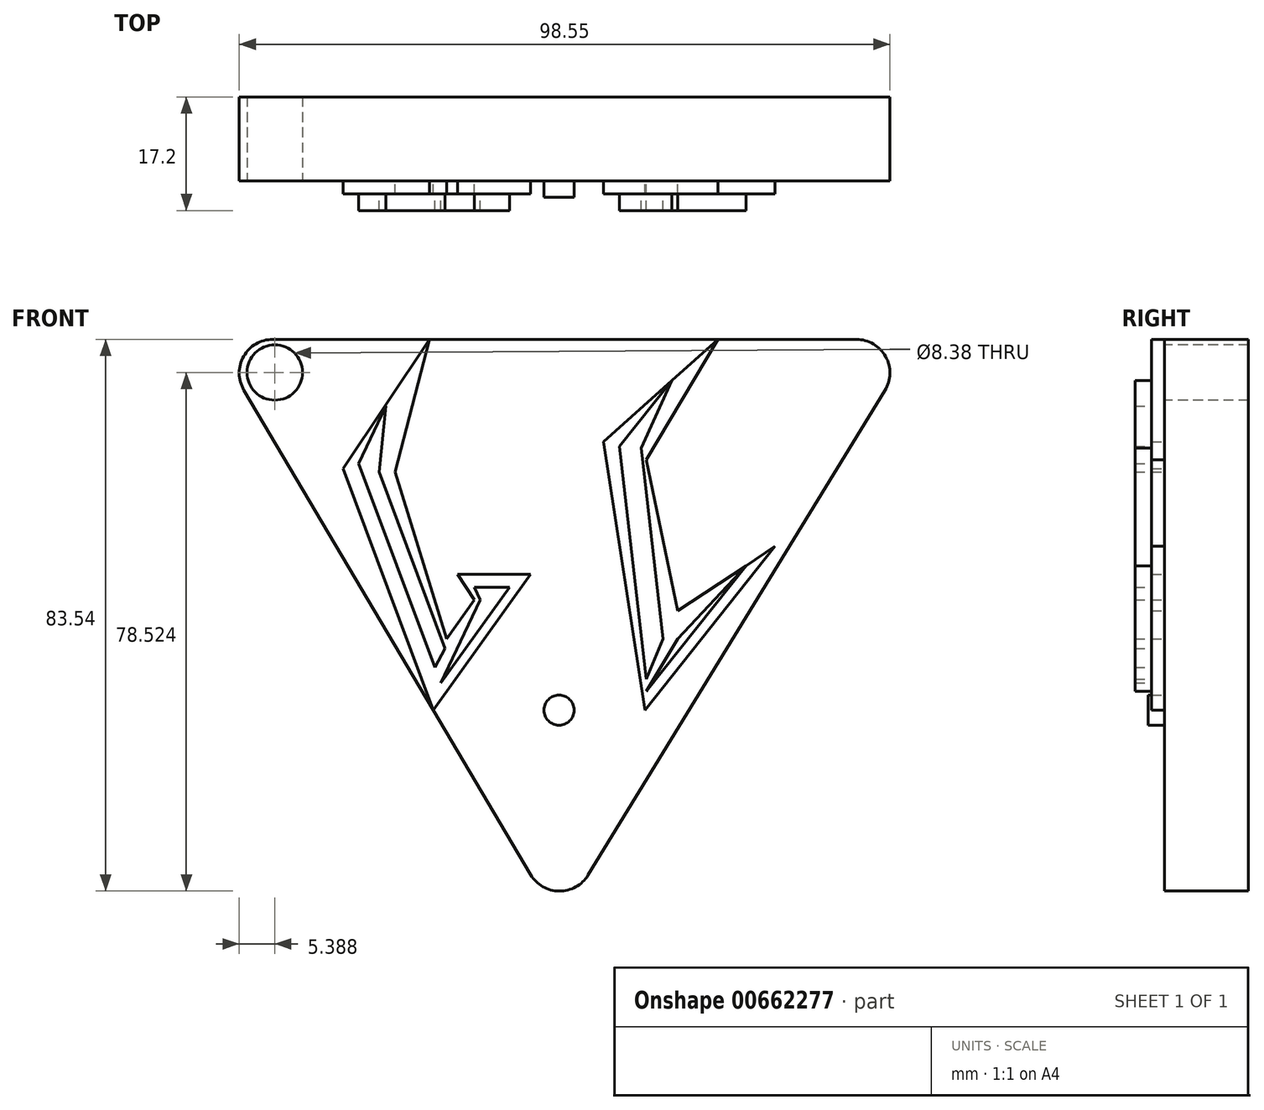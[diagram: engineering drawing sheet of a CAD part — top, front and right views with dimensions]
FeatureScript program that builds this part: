
annotation { "Feature Type Name" : "Feature", "Feature Type Description" : "" }
export const myFeature = defineFeature(function(context is Context, id is Id, definition is map)
    precondition{}
    {
        {
            var Q0;
            Q0=qCreatedBy(makeId("Front.planeOp"),FACE);
            var sketch = newSketch(context, id + "F0", { "sketchPlane" : qUnion([Q0])});
            skLineSegment(sketch, "E0", {"start": v(-52.26, 56.14) * mm, "end": v(54.1, 56.14) * mm});
            skLineSegment(sketch, "E1", {"start": v(54.1, 56.14) * mm, "end": v(0, -32.17) * mm});
            skLineSegment(sketch, "E2", {"start": v(0, -32.17) * mm, "end": v(-52.26, 56.14) * mm});
            skSolve(sketch);
        }
        {
            var Q0;
            Q0 = qSketchRegion(id + "F0", true);
            extrude(context, id + "F1", {"entities" : qUnion([Q0]), "depth" : 12.7 * mm, "offsetDistance" : 25.4 * mm});
        }
        {
            var Q0;
            Q0=makeQuery(id+"F1.opExtrude","CAP_FACE",FACE,{"disambiguationData":[OSD([sQuery(id+"F0.wireOp",EDGE,"E0"),sQuery(id+"F0.wireOp",EDGE,"E1"),sQuery(id+"F0.wireOp",EDGE,"E2")])],"isStart":false});
            var sketch = newSketch(context, id + "F2", { "sketchPlane" : qUnion([Q0])});
            skCircle(sketch, "E3", {"center": v(-43.04, 51.12) * mm, "radius": 4.2 * mm});
            skSolve(sketch);
        }
        {
            var Q0;
            Q0=makeQuery(id+"F2.imprint","IMPRINT",FACE,{"disambiguationData":[TD([[makeQuery(id+"F2.imprint","IMPRINT",EDGE,{"derivedFrom":sQuery(id+"F2.wireOp",EDGE,"E3")}),1.0]])]});
            var Q1;
            Q1=sQuery(id+"F2.wireOp",EDGE,"E3");
            extrude(context, id + "F3", {"entities" : qUnion([Q0]), "operationType" : NewBodyOperationType.REMOVE, "surfaceEntities" : qUnion([Q1]), "endBound" : BoundingType.THROUGH_ALL, "oppositeDirection" : true, "depth" : 25.4 * mm, "offsetDistance" : 25.4 * mm});
        }
        {
            var Q0;
            Q0=makeQuery(id+"F1.opExtrude","SWEPT_EDGE",EDGE,{"disambiguationData":[OSD([sQuery(id+"F0.wireOp",EDGE,"E0"),sQuery(id+"F0.wireOp",EDGE,"E1")])]});
            var Q1;
            Q1=makeQuery(id+"F1.opExtrude","SWEPT_EDGE",EDGE,{"disambiguationData":[OSD([sQuery(id+"F0.wireOp",EDGE,"E1"),sQuery(id+"F0.wireOp",EDGE,"E2")])]});
            var Q2;
            Q2=makeQuery(id+"F1.opExtrude","SWEPT_EDGE",EDGE,{"disambiguationData":[OSD([sQuery(id+"F0.wireOp",EDGE,"E0"),sQuery(id+"F0.wireOp",EDGE,"E2")])]});
            fillet(context, id + "F4", {"entities" : qUnion([Q0, Q1, Q2]), "radius" : 5.08 * mm, "tangentPropagation" : true, "allowEdgeOverflow" : false});
        }
        {
            var Q0;
            Q0=makeQuery(id+"F1.opExtrude","CAP_FACE",FACE,{"disambiguationData":[OSD([sQuery(id+"F0.wireOp",EDGE,"E0"),sQuery(id+"F0.wireOp",EDGE,"E1"),sQuery(id+"F0.wireOp",EDGE,"E2")])],"isStart":false});
            var sketch = newSketch(context, id + "F5", { "sketchPlane" : qUnion([Q0])});
            skLineSegment(sketch, "E4", {"start": v(-19.63, 56.14) * mm, "end": v(-32.72, 36.6) * mm});
            skLineSegment(sketch, "E5", {"start": v(-32.72, 36.6) * mm, "end": v(-19.04, 0) * mm});
            skLineSegment(sketch, "E6", {"start": v(-19.04, 0) * mm, "end": v(-4.3, 20.56) * mm});
            skLineSegment(sketch, "E7", {"start": v(-4.3, 20.56) * mm, "end": v(-15.4, 20.56) * mm});
            skLineSegment(sketch, "E8", {"start": v(-15.4, 20.56) * mm, "end": v(-12.81, 16.68) * mm});
            skLineSegment(sketch, "E9", {"start": v(-12.81, 16.68) * mm, "end": v(-17.04, 10.8) * mm});
            skLineSegment(sketch, "E10", {"start": v(-17.04, 10.8) * mm, "end": v(-24.8, 36.04) * mm});
            skLineSegment(sketch, "E11", {"start": v(-24.8, 36.04) * mm, "end": v(-19.63, 56.14) * mm});
            skSolve(sketch);
        }
        {
            var Q0;
            Q0 = qSketchRegion(id + "F5", true);
            extrude(context, id + "F6", {"entities" : qUnion([Q0]), "operationType" : NewBodyOperationType.ADD, "depth" : 2 * mm, "offsetDistance" : 25.4 * mm});
        }
        {
            var Q0;
            Q0=makeQuery(id+"F6.opExtrude","CAP_FACE",FACE,{"disambiguationData":[OSD([sQuery(id+"F5.wireOp",EDGE,"E4"),sQuery(id+"F5.wireOp",EDGE,"E5"),sQuery(id+"F5.wireOp",EDGE,"E6"),sQuery(id+"F5.wireOp",EDGE,"E7"),sQuery(id+"F5.wireOp",EDGE,"E8"),sQuery(id+"F5.wireOp",EDGE,"E9"),sQuery(id+"F5.wireOp",EDGE,"E10"),sQuery(id+"F5.wireOp",EDGE,"E11")])],"isStart":false});
            var sketch = newSketch(context, id + "F7", { "sketchPlane" : qUnion([Q0])});
            skLineSegment(sketch, "E12", {"start": v(-26.18, 46.09) * mm, "end": v(-30.33, 37.33) * mm});
            skPoint(sketch, "E12.startSnap0", {"position": v(-22.21, 46.09) * mm});
            skPoint(sketch, "E12.startSnap1", {"position": v(-26.18, 46.37) * mm});
            skLineSegment(sketch, "E13", {"start": v(-30.33, 37.33) * mm, "end": v(-18.79, 6.47) * mm});
            skLineSegment(sketch, "E14", {"start": v(-18.79, 6.47) * mm, "end": v(-17.24, 9.3) * mm});
            skLineSegment(sketch, "E15", {"start": v(-17.24, 9.3) * mm, "end": v(-27.23, 36.04) * mm});
            skLineSegment(sketch, "E16", {"start": v(-12.81, 18.62) * mm, "end": v(-7.47, 18.62) * mm});
            skPoint(sketch, "E16.startSnap0", {"position": v(-14.1, 18.62) * mm});
            skLineSegment(sketch, "E17", {"start": v(-7.47, 18.62) * mm, "end": v(-17.88, 4.1) * mm});
            skLineSegment(sketch, "E18", {"start": v(-17.88, 4.1) * mm, "end": v(-11.92, 16.68) * mm});
            skLineSegment(sketch, "E19", {"start": v(-11.92, 16.68) * mm, "end": v(-12.81, 18.62) * mm});
            skLineSegment(sketch, "E20", {"start": v(-27.23, 36.04) * mm, "end": v(-26.18, 46.37) * mm});
            skSolve(sketch);
        }
        {
            var Q0;
            Q0 = qSketchRegion(id + "F7", true);
            extrude(context, id + "F8", {"entities" : qUnion([Q0]), "operationType" : NewBodyOperationType.ADD, "depth" : 2.5 * mm, "offsetDistance" : 25.4 * mm});
        }
        {
            var Q0;
            {var subQ0=sQuery(id+"F0.wireOp",EDGE,"E1");var subQ1=sQuery(id+"F0.wireOp",EDGE,"E0");var subQ2=sQuery(id+"F0.wireOp",EDGE,"E2");var subQ3=makeQuery(id+"F1.opExtrude","CAP_FACE",FACE,{"disambiguationData":[OSD([subQ1,subQ0,subQ2])],"isStart":false});Q0=makeQuery(id+"F6.boolean.opBoolean","SPLIT",FACE,{"disambiguationData":[TD([makeQuery(id+"F1.opExtrude","SWEPT_FACE",FACE,{"disambiguationData":[OSD([subQ0])]})])],"derivedFrom":subQ3});}
            var sketch = newSketch(context, id + "F9", { "sketchPlane" : qUnion([Q0])});
            skCircle(sketch, "E21", {"center": v(0, 0) * mm, "radius": 2.28 * mm});
            skSolve(sketch);
        }
        {
            var Q0;
            Q0 = qSketchRegion(id + "F9", true);
            extrude(context, id + "F10", {"entities" : qUnion([Q0]), "operationType" : NewBodyOperationType.ADD, "depth" : 2.5 * mm, "offsetDistance" : 25.4 * mm});
        }
        {
            var Q0;
            {var subQ0=sQuery(id+"F0.wireOp",EDGE,"E1");var subQ1=sQuery(id+"F0.wireOp",EDGE,"E0");var subQ2=sQuery(id+"F0.wireOp",EDGE,"E2");var subQ3=makeQuery(id+"F1.opExtrude","CAP_FACE",FACE,{"disambiguationData":[OSD([subQ1,subQ0,subQ2])],"isStart":false});Q0=makeQuery(id+"F6.boolean.opBoolean","SPLIT",FACE,{"disambiguationData":[TD([makeQuery(id+"F1.opExtrude","SWEPT_FACE",FACE,{"disambiguationData":[OSD([subQ0])]})])],"derivedFrom":subQ3});}
            var sketch = newSketch(context, id + "F11", { "sketchPlane" : qUnion([Q0])});
            skLineSegment(sketch, "E22", {"start": v(24.06, 56.14) * mm, "end": v(6.73, 40.65) * mm});
            skLineSegment(sketch, "E23", {"start": v(6.73, 40.65) * mm, "end": v(13, 0) * mm});
            skLineSegment(sketch, "E24", {"start": v(13, 0) * mm, "end": v(32.72, 24.8) * mm});
            skLineSegment(sketch, "E25", {"start": v(32.72, 24.8) * mm, "end": v(17.97, 15.02) * mm});
            skLineSegment(sketch, "E26", {"start": v(17.97, 15.02) * mm, "end": v(13.18, 37.88) * mm});
            skLineSegment(sketch, "E27", {"start": v(13.18, 37.88) * mm, "end": v(24.06, 56.14) * mm});
            skSolve(sketch);
        }
        {
            var Q0;
            Q0 = qSketchRegion(id + "F11", true);
            extrude(context, id + "F12", {"entities" : qUnion([Q0]), "operationType" : NewBodyOperationType.ADD, "depth" : 2 * mm, "offsetDistance" : 25.4 * mm});
        }
        {
            var Q0;
            Q0=makeQuery(id+"F12.opExtrude","CAP_FACE",FACE,{"disambiguationData":[OSD([sQuery(id+"F11.wireOp",EDGE,"E22"),sQuery(id+"F11.wireOp",EDGE,"E23"),sQuery(id+"F11.wireOp",EDGE,"E24"),sQuery(id+"F11.wireOp",EDGE,"E25"),sQuery(id+"F11.wireOp",EDGE,"E26"),sQuery(id+"F11.wireOp",EDGE,"E27")])],"isStart":false});
            var sketch = newSketch(context, id + "F13", { "sketchPlane" : qUnion([Q0])});
            skLineSegment(sketch, "E28", {"start": v(17.1, 49.91) * mm, "end": v(9.13, 39.91) * mm});
            skLineSegment(sketch, "E29", {"start": v(9.13, 39.91) * mm, "end": v(13.18, 4.7) * mm});
            skLineSegment(sketch, "E30", {"start": v(13.18, 4.7) * mm, "end": v(15.76, 10.78) * mm});
            skLineSegment(sketch, "E31", {"start": v(15.76, 10.78) * mm, "end": v(12.44, 39.65) * mm});
            skLineSegment(sketch, "E32", {"start": v(12.44, 39.65) * mm, "end": v(17.1, 49.91) * mm});
            skLineSegment(sketch, "E33", {"start": v(17.97, 10.78) * mm, "end": v(28.29, 21.86) * mm});
            skLineSegment(sketch, "E34", {"start": v(28.29, 21.86) * mm, "end": v(13.18, 2.87) * mm});
            skLineSegment(sketch, "E35", {"start": v(13.18, 2.87) * mm, "end": v(17.97, 10.78) * mm});
            skSolve(sketch);
        }
        {
            var Q0;
            Q0 = qSketchRegion(id + "F13", true);
            extrude(context, id + "F14", {"entities" : qUnion([Q0]), "operationType" : NewBodyOperationType.ADD, "depth" : 2.5 * mm, "offsetDistance" : 25.4 * mm});
        }
    });
